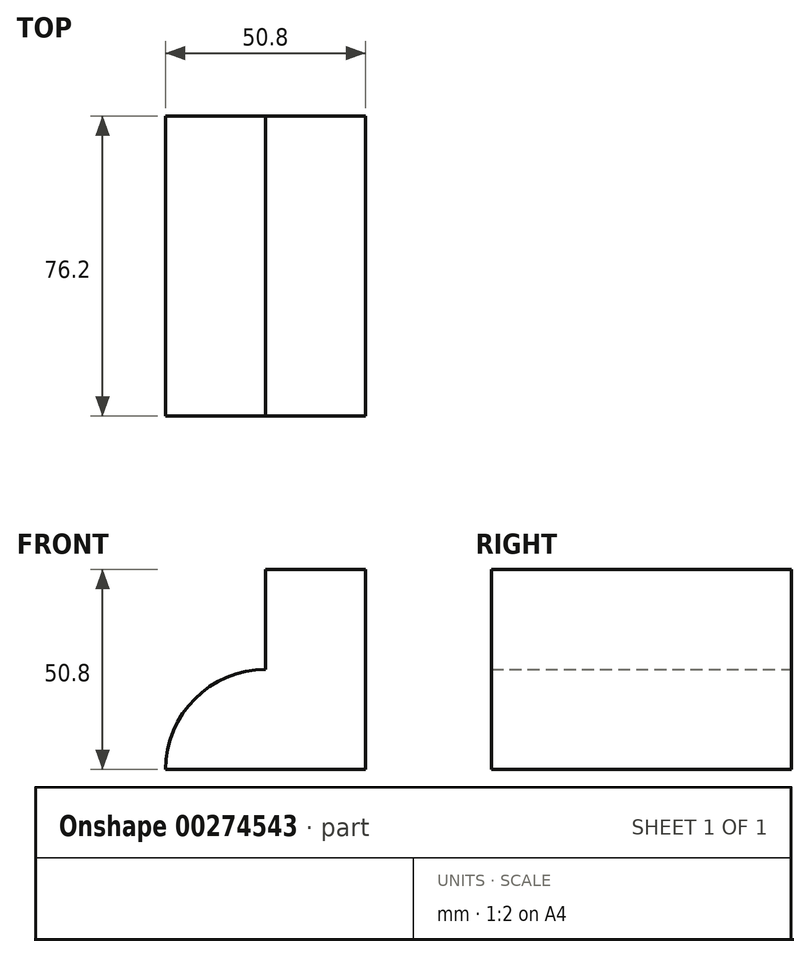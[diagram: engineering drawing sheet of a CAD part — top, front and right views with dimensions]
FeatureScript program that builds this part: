
annotation { "Feature Type Name" : "Feature", "Feature Type Description" : "" }
export const myFeature = defineFeature(function(context is Context, id is Id, definition is map)
    precondition{}
    {
        {
            var Q0;
            Q0=qCreatedBy(makeId("Front.planeOp"),FACE);
            var sketch = newSketch(context, id + "F0", { "sketchPlane" : qUnion([Q0])});
            skLineSegment(sketch, "E0", {"start": v(0, 0) * mm, "end": v(0, 50.8) * mm});
            skLineSegment(sketch, "E1", {"start": v(0, 50.8) * mm, "end": v(-25.4, 50.8) * mm});
            skLineSegment(sketch, "E2", {"start": v(-25.4, 50.8) * mm, "end": v(-25.4, 25.4) * mm});
            skLineSegment(sketch, "E3", {"start": v(-50.8, 0) * mm, "end": v(0, 0) * mm});
            skArc(sketch, "E4", {"start": v(-25.4, 25.4) * mm, "mid": v(-43.36, 17.96) * mm, "end": v(-50.8, 0) * mm});
            skSolve(sketch);
        }
        {
            var Q0;
            Q0 = qSketchRegion(id + "F0", true);
            extrude(context, id + "F1", {"entities" : qUnion([Q0]), "depth" : 76.2 * mm});
        }
    });
